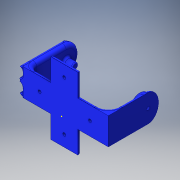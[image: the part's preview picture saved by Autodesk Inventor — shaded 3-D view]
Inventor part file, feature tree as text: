
AUTODESK INVENTOR PART (.ipt)
format: ipt  version: 2016 (Build 200138000, 138)  size: 571,904 bytes
history: native  units: in
note: dims shown in document units (in); Inventor stores cm internally (conversion verified against a paired STEP export)
features: sketch x12, other x3
ambient origin geometry x8: Origin, YZ Plane, XZ Plane, XY Plane, X Axis, Y Axis, Z Axis, Center Point
bodies: Solid1 (feature_tree)
feature tree (15):
  other  "Ankle.ipt"
  other  "Solid1::Ankle.ipt"
  other  "TaggingFeature1"
  sketch  "Sketch1"  dims[d0=0.3937in]
  sketch  "Sketch4"
  sketch  "Sketch5"
  sketch  "Sketch7"
  sketch  "Sketch9"
  sketch  "Sketch10"
  sketch  "Sketch15"
  sketch  "Sketch16"
  sketch  "Sketch17"
  sketch  "Sketch18"
  sketch  "Sketch19"
  sketch  "Sketch20"
